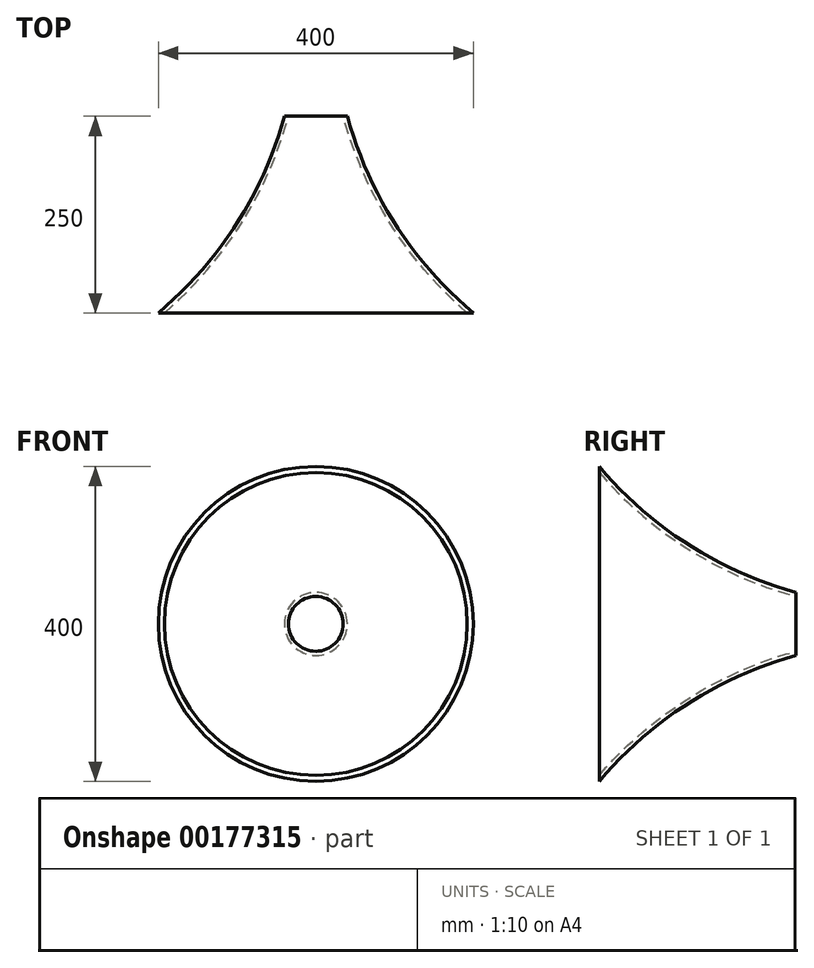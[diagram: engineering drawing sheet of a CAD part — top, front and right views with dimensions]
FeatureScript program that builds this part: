
annotation { "Feature Type Name" : "Feature", "Feature Type Description" : "" }
export const myFeature = defineFeature(function(context is Context, id is Id, definition is map)
    precondition{}
    {
        {
            var Q0;
            Q0=qCreatedBy(makeId("Front.planeOp"),FACE);
            var sketch = newSketch(context, id + "F0", { "sketchPlane" : qUnion([Q0])});
            skCircle(sketch, "E0", {"center": v(0, 0) * mm, "radius": 40 * mm});
            skSolve(sketch);
        }
        {
            var Q0;
            Q0=qCreatedBy(makeId("Front.planeOp"),FACE);
            cPlane(context, id + "F1", {"entities" : qUnion([Q0]), "cplaneType" : CPlaneType.OFFSET, "offset" : 250 * mm, "width" : 150 * mm, "height" : 150 * mm});
        }
        {
            var Q0;
            Q0=qCreatedBy(id+"F1.planeOp",FACE);
            var sketch = newSketch(context, id + "F2", { "sketchPlane" : qUnion([Q0])});
            skCircle(sketch, "E1", {"center": v(0, 0) * mm, "radius": 200 * mm});
            skSolve(sketch);
        }
        {
            var Q0;
            Q0=qCreatedBy(makeId("Right.planeOp"),FACE);
            var sketch = newSketch(context, id + "F3", { "sketchPlane" : qUnion([Q0])});
            skArc(sketch, "E2", {"start": v(-250, 200) * mm, "mid": v(-137.15, 101.02) * mm, "end": v(0, 40) * mm});
            skSolve(sketch);
        }
        {
            var Q0;
            Q0=makeQuery(id+"F0.imprint","IMPRINT",FACE,{"disambiguationData":[TD([[makeQuery(id+"F0.imprint","IMPRINT",EDGE,{"derivedFrom":sQuery(id+"F0.wireOp",EDGE,"E0")}),1.0]])]});
            var Q1;
            Q1=makeQuery(id+"F2.imprint","IMPRINT",FACE,{"disambiguationData":[TD([[makeQuery(id+"F2.imprint","IMPRINT",EDGE,{"derivedFrom":sQuery(id+"F2.wireOp",EDGE,"E1")}),1.0]])]});
            var Q2;
            Q2=sQuery(id+"F3.wireOp",EDGE,"E2");
            loft(context, id + "F4", {"addGuides" : true, "sheetProfilesArray" : [{ "sheetProfileEntities" : qUnion([Q0]) }, { "sheetProfileEntities" : qUnion([Q1]) }], "guidesArray" : [{ "guideEntities" : qUnion([Q2]), "guideDerivativeType" : LoftGuideDerivativeType.DEFAULT, "guideDerivativeMagnitude" : 1 }]});
        }
        {
            var Q0;
            Q0=makeQuery(id+"F4.opLoft","CAP_FACE",FACE,{"disambiguationData":[OSD([makeQuery(id+"F2.imprint","IMPRINT",FACE,{"disambiguationData":[TD([[makeQuery(id+"F2.imprint","IMPRINT",EDGE,{"derivedFrom":sQuery(id+"F2.wireOp",EDGE,"E1")}),1.0]])]})])],"isStart":true});
            var Q1;
            Q1=makeQuery(id+"F4.opLoft","CAP_FACE",FACE,{"disambiguationData":[OSD([makeQuery(id+"F0.imprint","IMPRINT",FACE,{"disambiguationData":[TD([[makeQuery(id+"F0.imprint","IMPRINT",EDGE,{"derivedFrom":sQuery(id+"F0.wireOp",EDGE,"E0")}),1.0]])]})])],"isStart":true});
            shell(context, id + "F5", {"entities" : qUnion([Q0, Q1]), "thickness" : 5 * mm});
        }
    });
